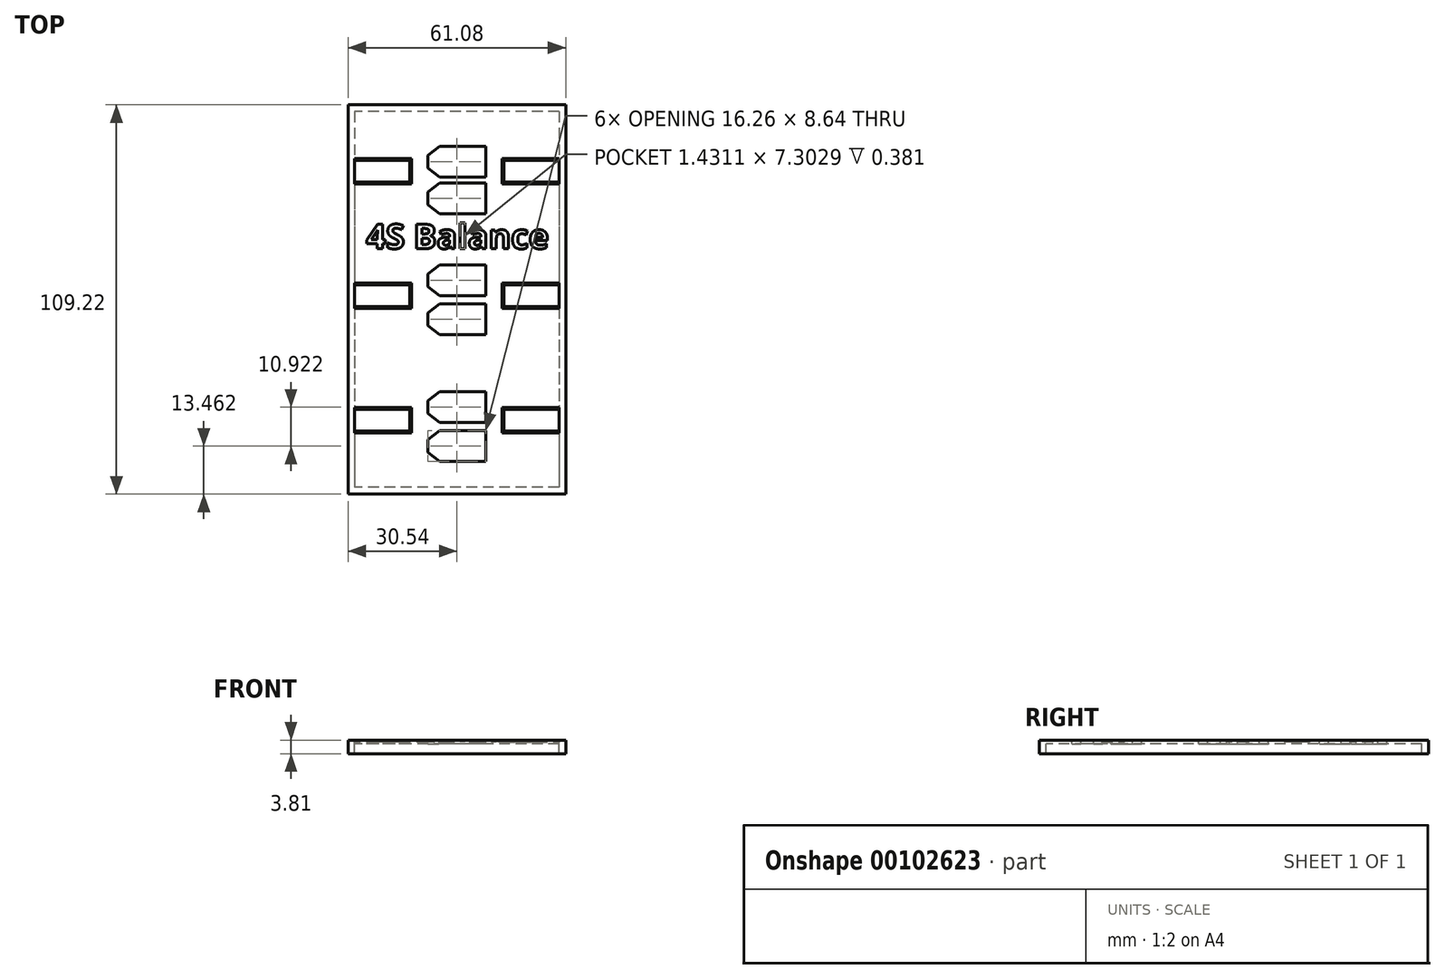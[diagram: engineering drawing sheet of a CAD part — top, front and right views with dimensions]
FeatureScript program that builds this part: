
annotation { "Feature Type Name" : "Feature", "Feature Type Description" : "" }
export const myFeature = defineFeature(function(context is Context, id is Id, definition is map)
    precondition{}
    {
        {
            var Q0;
            Q0=qCreatedBy(makeId("Top.planeOp"),FACE);
            var sketch = newSketch(context, id + "F0", { "sketchPlane" : qUnion([Q0])});
            skLineSegment(sketch, "E0.bottom", {"start": v(30.54, 54.61) * mm, "end": v(-30.54, 54.6) * mm});
            skLineSegment(sketch, "E0.top", {"start": v(30.54, -54.6) * mm, "end": v(-30.54, -54.61) * mm});
            skLineSegment(sketch, "E0.left", {"start": v(30.54, 54.61) * mm, "end": v(30.54, -54.6) * mm});
            skLineSegment(sketch, "E0.right", {"start": v(-30.54, 54.6) * mm, "end": v(-30.54, -54.61) * mm});
            skPoint(sketch, "E0.middle", {"position": v(0, 0) * mm});
            skLineSegment(sketch, "E1.bottom", {"start": v(28.7, 52.7) * mm, "end": v(-28.7, 52.7) * mm});
            skLineSegment(sketch, "E1.top", {"start": v(28.7, -52.7) * mm, "end": v(-28.7, -52.7) * mm});
            skLineSegment(sketch, "E1.left", {"start": v(28.7, 52.7) * mm, "end": v(28.7, -52.7) * mm});
            skLineSegment(sketch, "E1.right", {"start": v(-28.7, 52.7) * mm, "end": v(-28.7, -52.7) * mm});
            skLineSegment(sketch, "E2.bottom", {"start": v(8.13, -36.83) * mm, "end": v(-8.13, -36.83) * mm});
            skLineSegment(sketch, "E2.top", {"start": v(8.13, -45.47) * mm, "end": v(-8.13, -45.47) * mm});
            skLineSegment(sketch, "E2.left", {"start": v(8.13, -36.83) * mm, "end": v(8.13, -45.47) * mm});
            skLineSegment(sketch, "E2.right", {"start": v(-8.13, -36.83) * mm, "end": v(-8.13, -45.47) * mm});
            skPoint(sketch, "E2.middle", {"position": v(0, -41.15) * mm});
            skLineSegment(sketch, "E3.bottom", {"start": v(8.13, -34.54) * mm, "end": v(-8.13, -34.54) * mm});
            skLineSegment(sketch, "E3.top", {"start": v(8.13, -25.9) * mm, "end": v(-8.13, -25.9) * mm});
            skLineSegment(sketch, "E3.left", {"start": v(8.13, -34.54) * mm, "end": v(8.13, -25.9) * mm});
            skLineSegment(sketch, "E3.right", {"start": v(-8.13, -34.54) * mm, "end": v(-8.13, -25.9) * mm});
            skPoint(sketch, "E3.middle", {"position": v(0, -30.23) * mm});
            skLineSegment(sketch, "E4.bottom", {"start": v(8.13, -9.9) * mm, "end": v(-8.13, -9.9) * mm});
            skLineSegment(sketch, "E4.top", {"start": v(8.13, -1.27) * mm, "end": v(-8.13, -1.27) * mm});
            skLineSegment(sketch, "E4.left", {"start": v(8.13, -9.9) * mm, "end": v(8.13, -1.27) * mm});
            skLineSegment(sketch, "E4.right", {"start": v(-8.13, -9.9) * mm, "end": v(-8.13, -1.27) * mm});
            skPoint(sketch, "E4.middle", {"position": v(0, -5.59) * mm});
            skLineSegment(sketch, "E5.bottom", {"start": v(8.13, 1.02) * mm, "end": v(-8.13, 1.02) * mm});
            skLineSegment(sketch, "E5.top", {"start": v(8.13, 9.65) * mm, "end": v(-8.13, 9.65) * mm});
            skLineSegment(sketch, "E5.left", {"start": v(8.13, 1.02) * mm, "end": v(8.13, 9.65) * mm});
            skLineSegment(sketch, "E5.right", {"start": v(-8.13, 1.02) * mm, "end": v(-8.13, 9.65) * mm});
            skPoint(sketch, "E5.middle", {"position": v(0, 5.33) * mm});
            skLineSegment(sketch, "E6.bottom", {"start": v(8.13, 24) * mm, "end": v(-8.13, 24) * mm});
            skLineSegment(sketch, "E6.top", {"start": v(8.13, 32.64) * mm, "end": v(-8.13, 32.64) * mm});
            skLineSegment(sketch, "E6.left", {"start": v(8.13, 24) * mm, "end": v(8.13, 32.64) * mm});
            skLineSegment(sketch, "E6.right", {"start": v(-8.13, 24) * mm, "end": v(-8.13, 32.64) * mm});
            skPoint(sketch, "E6.middle", {"position": v(0, 28.32) * mm});
            skLineSegment(sketch, "E7.bottom", {"start": v(8.13, 34.29) * mm, "end": v(-8.13, 34.29) * mm});
            skLineSegment(sketch, "E7.top", {"start": v(8.13, 42.93) * mm, "end": v(-8.13, 42.93) * mm});
            skLineSegment(sketch, "E7.left", {"start": v(8.13, 34.3) * mm, "end": v(8.13, 42.93) * mm});
            skLineSegment(sketch, "E7.right", {"start": v(-8.13, 34.3) * mm, "end": v(-8.13, 42.93) * mm});
            skPoint(sketch, "E7.middle", {"position": v(0, 38.6) * mm});
            skLineSegment(sketch, "E8", {"start": v(-4.83, -45.47) * mm, "end": v(-8.13, -42.93) * mm});
            skLineSegment(sketch, "E9", {"start": v(-8.13, -39.37) * mm, "end": v(-4.83, -36.83) * mm});
            skLineSegment(sketch, "E10", {"start": v(-4.83, -34.54) * mm, "end": v(-8.13, -32) * mm});
            skLineSegment(sketch, "E11", {"start": v(-8.13, -28.45) * mm, "end": v(-4.83, -25.9) * mm});
            skLineSegment(sketch, "E12", {"start": v(-4.83, -9.9) * mm, "end": v(-8.13, -7.37) * mm});
            skLineSegment(sketch, "E13", {"start": v(-8.13, -3.81) * mm, "end": v(-4.83, -1.27) * mm});
            skLineSegment(sketch, "E14", {"start": v(-4.83, 1.02) * mm, "end": v(-8.13, 3.56) * mm});
            skLineSegment(sketch, "E15", {"start": v(-8.13, 7.11) * mm, "end": v(-4.83, 9.65) * mm});
            skLineSegment(sketch, "E16", {"start": v(-4.83, 24) * mm, "end": v(-8.13, 26.54) * mm});
            skLineSegment(sketch, "E17", {"start": v(-8.13, 30.1) * mm, "end": v(-4.83, 32.64) * mm});
            skLineSegment(sketch, "E18", {"start": v(-4.83, 34.3) * mm, "end": v(-8.13, 36.83) * mm});
            skLineSegment(sketch, "E19", {"start": v(-8.13, 40.39) * mm, "end": v(-4.83, 42.93) * mm});
            skLineSegment(sketch, "E20.bottom", {"start": v(28.7, -2.03) * mm, "end": v(13.2, -2.03) * mm});
            skLineSegment(sketch, "E20.top", {"start": v(28.7, 4.06) * mm, "end": v(13.2, 4.06) * mm});
            skLineSegment(sketch, "E20.left", {"start": v(28.7, -2.03) * mm, "end": v(28.7, 4.06) * mm});
            skLineSegment(sketch, "E20.right", {"start": v(13.2, -2.03) * mm, "end": v(13.2, 4.06) * mm});
            skPoint(sketch, "E20.middle", {"position": v(20.96, 1.02) * mm});
            skLineSegment(sketch, "E21.bottom", {"start": v(28.7, 32.9) * mm, "end": v(13.2, 32.9) * mm});
            skLineSegment(sketch, "E21.top", {"start": v(28.7, 38.99) * mm, "end": v(13.2, 38.99) * mm});
            skLineSegment(sketch, "E21.left", {"start": v(28.7, 32.9) * mm, "end": v(28.7, 38.99) * mm});
            skLineSegment(sketch, "E21.right", {"start": v(13.2, 32.9) * mm, "end": v(13.2, 38.99) * mm});
            skPoint(sketch, "E21.middle", {"position": v(20.95, 35.94) * mm});
            skLineSegment(sketch, "E22.bottom", {"start": v(28.7, -30.86) * mm, "end": v(13.2, -30.86) * mm});
            skLineSegment(sketch, "E22.top", {"start": v(28.7, -36.96) * mm, "end": v(13.2, -36.96) * mm});
            skLineSegment(sketch, "E22.left", {"start": v(28.7, -30.86) * mm, "end": v(28.7, -36.96) * mm});
            skLineSegment(sketch, "E22.right", {"start": v(13.2, -30.86) * mm, "end": v(13.2, -36.96) * mm});
            skPoint(sketch, "E22.middle", {"position": v(20.96, -33.9) * mm});
            skLineSegment(sketch, "E23.bottom", {"start": v(-13.2, -30.86) * mm, "end": v(-28.7, -30.86) * mm});
            skLineSegment(sketch, "E23.top", {"start": v(-13.2, -36.96) * mm, "end": v(-28.7, -36.96) * mm});
            skLineSegment(sketch, "E23.left", {"start": v(-13.2, -30.86) * mm, "end": v(-13.2, -36.96) * mm});
            skLineSegment(sketch, "E23.right", {"start": v(-28.7, -30.86) * mm, "end": v(-28.7, -36.96) * mm});
            skPoint(sketch, "E23.middle", {"position": v(-20.96, -33.9) * mm});
            skLineSegment(sketch, "E24.bottom", {"start": v(-13.2, 4.06) * mm, "end": v(-28.7, 4.06) * mm});
            skLineSegment(sketch, "E24.top", {"start": v(-13.2, -2.03) * mm, "end": v(-28.7, -2.03) * mm});
            skLineSegment(sketch, "E24.left", {"start": v(-13.2, 4.06) * mm, "end": v(-13.2, -2.03) * mm});
            skLineSegment(sketch, "E24.right", {"start": v(-28.7, 4.06) * mm, "end": v(-28.7, -2.03) * mm});
            skPoint(sketch, "E24.middle", {"position": v(-20.95, 1.02) * mm});
            skLineSegment(sketch, "E25.bottom", {"start": v(-13.2, 38.99) * mm, "end": v(-28.7, 38.99) * mm});
            skLineSegment(sketch, "E25.top", {"start": v(-13.2, 32.9) * mm, "end": v(-28.7, 32.9) * mm});
            skLineSegment(sketch, "E25.left", {"start": v(-13.2, 38.99) * mm, "end": v(-13.2, 32.9) * mm});
            skLineSegment(sketch, "E25.right", {"start": v(-28.7, 38.99) * mm, "end": v(-28.7, 32.9) * mm});
            skPoint(sketch, "E25.middle", {"position": v(-20.95, 35.94) * mm});
            skSolve(sketch);
        }
        {
            var Q0;
            Q0=makeQuery(id+"F0.imprint","IMPRINT",FACE,{"disambiguationData":[TD([[makeQuery(id+"F0.imprint","IMPRINT",EDGE,{"derivedFrom":sQuery(id+"F0.wireOp",EDGE,"E1.bottom")}),1.0]])]});
            var Q1;
            {var subQ3=sQuery(id+"F0.wireOp",EDGE,"E8");Q1=makeQuery(id+"F0.imprint","IMPRINT",FACE,{"disambiguationData":[TD([[makeQuery(id+"F0.imprint","IMPRINT",EDGE,{"derivedFrom":subQ3}),1.0]])]});}
            var Q2;
            {var subQ3=sQuery(id+"F0.wireOp",EDGE,"E9");Q2=makeQuery(id+"F0.imprint","IMPRINT",FACE,{"disambiguationData":[TD([[makeQuery(id+"F0.imprint","IMPRINT",EDGE,{"derivedFrom":subQ3}),1.0]])]});}
            var Q3;
            {var subQ3=sQuery(id+"F0.wireOp",EDGE,"E10");Q3=makeQuery(id+"F0.imprint","IMPRINT",FACE,{"disambiguationData":[TD([[makeQuery(id+"F0.imprint","IMPRINT",EDGE,{"derivedFrom":subQ3}),1.0]])]});}
            var Q4;
            {var subQ3=sQuery(id+"F0.wireOp",EDGE,"E11");Q4=makeQuery(id+"F0.imprint","IMPRINT",FACE,{"disambiguationData":[TD([[makeQuery(id+"F0.imprint","IMPRINT",EDGE,{"derivedFrom":subQ3}),1.0]])]});}
            var Q5;
            {var subQ3=sQuery(id+"F0.wireOp",EDGE,"E12");Q5=makeQuery(id+"F0.imprint","IMPRINT",FACE,{"disambiguationData":[TD([[makeQuery(id+"F0.imprint","IMPRINT",EDGE,{"derivedFrom":subQ3}),1.0]])]});}
            var Q6;
            {var subQ3=sQuery(id+"F0.wireOp",EDGE,"E13");Q6=makeQuery(id+"F0.imprint","IMPRINT",FACE,{"disambiguationData":[TD([[makeQuery(id+"F0.imprint","IMPRINT",EDGE,{"derivedFrom":subQ3}),1.0]])]});}
            var Q7;
            {var subQ3=sQuery(id+"F0.wireOp",EDGE,"E14");Q7=makeQuery(id+"F0.imprint","IMPRINT",FACE,{"disambiguationData":[TD([[makeQuery(id+"F0.imprint","IMPRINT",EDGE,{"derivedFrom":subQ3}),1.0]])]});}
            var Q8;
            {var subQ3=sQuery(id+"F0.wireOp",EDGE,"E15");Q8=makeQuery(id+"F0.imprint","IMPRINT",FACE,{"disambiguationData":[TD([[makeQuery(id+"F0.imprint","IMPRINT",EDGE,{"derivedFrom":subQ3}),1.0]])]});}
            var Q9;
            {var subQ3=sQuery(id+"F0.wireOp",EDGE,"E16");Q9=makeQuery(id+"F0.imprint","IMPRINT",FACE,{"disambiguationData":[TD([[makeQuery(id+"F0.imprint","IMPRINT",EDGE,{"derivedFrom":subQ3}),1.0]])]});}
            var Q10;
            {var subQ3=sQuery(id+"F0.wireOp",EDGE,"E17");Q10=makeQuery(id+"F0.imprint","IMPRINT",FACE,{"disambiguationData":[TD([[makeQuery(id+"F0.imprint","IMPRINT",EDGE,{"derivedFrom":subQ3}),1.0]])]});}
            var Q11;
            {var subQ3=sQuery(id+"F0.wireOp",EDGE,"E18");Q11=makeQuery(id+"F0.imprint","IMPRINT",FACE,{"disambiguationData":[TD([[makeQuery(id+"F0.imprint","IMPRINT",EDGE,{"derivedFrom":subQ3}),1.0]])]});}
            var Q12;
            {var subQ3=sQuery(id+"F0.wireOp",EDGE,"E19");Q12=makeQuery(id+"F0.imprint","IMPRINT",FACE,{"disambiguationData":[TD([[makeQuery(id+"F0.imprint","IMPRINT",EDGE,{"derivedFrom":subQ3}),1.0]])]});}
            extrude(context, id + "F1", {"entities" : qUnion([Q0, Q1, Q2, Q3, Q4, Q5, Q6, Q7, Q8, Q9, Q10, Q11, Q12]), "oppositeDirection" : true, "depth" : 1.02 * mm});
        }
        {
            var Q0;
            Q0=makeQuery(id+"F0.imprint","IMPRINT",FACE,{"disambiguationData":[TD([[makeQuery(id+"F0.imprint","IMPRINT",EDGE,{"derivedFrom":sQuery(id+"F0.wireOp",EDGE,"E0.bottom")}),1.0]])]});
            extrude(context, id + "F2", {"entities" : qUnion([Q0]), "operationType" : NewBodyOperationType.ADD, "oppositeDirection" : true, "depth" : 3.8 * mm});
        }
        {
            var Q0;
            {var subQ0=sQuery(id+"F0.wireOp",EDGE,"E25.top");var subQ1=sQuery(id+"F0.wireOp",EDGE,"E25.bottom");var subQ2=sQuery(id+"F0.wireOp",EDGE,"E24.top");var subQ3=sQuery(id+"F0.wireOp",EDGE,"E24.bottom");var subQ4=sQuery(id+"F0.wireOp",EDGE,"E23.top");var subQ5=sQuery(id+"F0.wireOp",EDGE,"E23.bottom");var subQ6=sQuery(id+"F0.wireOp",EDGE,"E22.top");var subQ7=sQuery(id+"F0.wireOp",EDGE,"E22.bottom");var subQ8=sQuery(id+"F0.wireOp",EDGE,"E21.top");var subQ9=sQuery(id+"F0.wireOp",EDGE,"E21.bottom");var subQ10=sQuery(id+"F0.wireOp",EDGE,"E20.top");var subQ11=sQuery(id+"F0.wireOp",EDGE,"E20.bottom");var subQ12=sQuery(id+"F0.wireOp",EDGE,"E1.right");var subQ13=sQuery(id+"F0.wireOp",EDGE,"E1.left");var subQ14=sQuery(id+"F0.wireOp",EDGE,"E1.top");var subQ15=sQuery(id+"F0.wireOp",EDGE,"E1.bottom");Q0=makeQuery(id+"F2.boolean.opBoolean","MERGE",FACE,{"derivedFrom":[makeQuery(id+"F1.opExtrude","CAP_FACE",FACE,{"disambiguationData":[OSD([subQ15,subQ14,subQ13,subQ12,sQuery(id+"F0.wireOp",EDGE,"E2.bottom"),sQuery(id+"F0.wireOp",EDGE,"E2.top"),sQuery(id+"F0.wireOp",EDGE,"E2.left"),sQuery(id+"F0.wireOp",EDGE,"E2.right"),sQuery(id+"F0.wireOp",EDGE,"E3.bottom"),sQuery(id+"F0.wireOp",EDGE,"E3.top"),sQuery(id+"F0.wireOp",EDGE,"E3.left"),sQuery(id+"F0.wireOp",EDGE,"E3.right"),sQuery(id+"F0.wireOp",EDGE,"E4.bottom"),sQuery(id+"F0.wireOp",EDGE,"E4.top"),sQuery(id+"F0.wireOp",EDGE,"E4.left"),sQuery(id+"F0.wireOp",EDGE,"E4.right"),sQuery(id+"F0.wireOp",EDGE,"E5.bottom"),sQuery(id+"F0.wireOp",EDGE,"E5.top"),sQuery(id+"F0.wireOp",EDGE,"E5.left"),sQuery(id+"F0.wireOp",EDGE,"E5.right"),sQuery(id+"F0.wireOp",EDGE,"E6.bottom"),sQuery(id+"F0.wireOp",EDGE,"E6.top"),sQuery(id+"F0.wireOp",EDGE,"E6.left"),sQuery(id+"F0.wireOp",EDGE,"E6.right"),sQuery(id+"F0.wireOp",EDGE,"E7.bottom"),sQuery(id+"F0.wireOp",EDGE,"E7.top"),sQuery(id+"F0.wireOp",EDGE,"E7.left"),sQuery(id+"F0.wireOp",EDGE,"E7.right"),sQuery(id+"F0.wireOp",EDGE,"E8"),sQuery(id+"F0.wireOp",EDGE,"E9"),sQuery(id+"F0.wireOp",EDGE,"E10"),sQuery(id+"F0.wireOp",EDGE,"E11"),sQuery(id+"F0.wireOp",EDGE,"E12"),sQuery(id+"F0.wireOp",EDGE,"E13"),sQuery(id+"F0.wireOp",EDGE,"E14"),sQuery(id+"F0.wireOp",EDGE,"E15"),sQuery(id+"F0.wireOp",EDGE,"E16"),sQuery(id+"F0.wireOp",EDGE,"E17"),sQuery(id+"F0.wireOp",EDGE,"E18"),sQuery(id+"F0.wireOp",EDGE,"E19"),subQ11,subQ10,sQuery(id+"F0.wireOp",EDGE,"E20.right"),subQ9,subQ8,sQuery(id+"F0.wireOp",EDGE,"E21.right"),subQ7,subQ6,sQuery(id+"F0.wireOp",EDGE,"E22.right"),subQ5,subQ4,sQuery(id+"F0.wireOp",EDGE,"E23.left"),subQ3,subQ2,sQuery(id+"F0.wireOp",EDGE,"E24.left"),subQ1,subQ0,sQuery(id+"F0.wireOp",EDGE,"E25.left")])],"isStart":true}),makeQuery(id+"F2.opExtrude","CAP_FACE",FACE,{"disambiguationData":[OSD([sQuery(id+"F0.wireOp",EDGE,"E0.bottom"),sQuery(id+"F0.wireOp",EDGE,"E0.top"),sQuery(id+"F0.wireOp",EDGE,"E0.left"),sQuery(id+"F0.wireOp",EDGE,"E0.right"),subQ15,subQ14,subQ13,subQ12,subQ11,subQ10,sQuery(id+"F0.wireOp",EDGE,"E20.left"),subQ9,subQ8,sQuery(id+"F0.wireOp",EDGE,"E21.left"),subQ7,subQ6,sQuery(id+"F0.wireOp",EDGE,"E22.left"),subQ5,subQ4,sQuery(id+"F0.wireOp",EDGE,"E23.right"),subQ3,subQ2,sQuery(id+"F0.wireOp",EDGE,"E24.right"),subQ1,subQ0,sQuery(id+"F0.wireOp",EDGE,"E25.right")])],"isStart":true})]});}
            var sketch = newSketch(context, id + "F3", { "sketchPlane" : qUnion([Q0])});
            skText(sketch, "E26", { "text": "4S Balance", "fontName": "OpenSans-Bold.ttf"});
            const initialGuessF3  = {"E26": [-0.0254, 0.01424, 1, 0, 0.00692]};
            skSetInitialGuess(sketch, initialGuessF3);
            skSolve(sketch);
        }
        {
            var Q0;
            Q0 = qSketchRegion(id + "F3", true);
            extrude(context, id + "F4", {"entities" : qUnion([Q0]), "operationType" : NewBodyOperationType.REMOVE, "oppositeDirection" : true, "depth" : 0.38 * mm});
        }
        {
            var Q0;
            {var subQ0=sQuery(id+"F0.wireOp",EDGE,"E20.top");Q0=makeQuery(id+"F2.boolean.opBoolean","MERGE",EDGE,{"derivedFrom":[makeQuery(id+"F1.opExtrude","CAP_EDGE",EDGE,{"disambiguationData":[OSD([subQ0])],"isStart":true}),makeQuery(id+"F2.opExtrude","CAP_EDGE",EDGE,{"disambiguationData":[OSD([subQ0])],"isStart":true})]});}
            var Q1;
            Q1=makeQuery(id+"F1.opExtrude","CAP_EDGE",EDGE,{"disambiguationData":[OSD([sQuery(id+"F0.wireOp",EDGE,"E20.right")])],"isStart":true});
            var Q2;
            {var subQ0=sQuery(id+"F0.wireOp",EDGE,"E20.bottom");Q2=makeQuery(id+"F2.boolean.opBoolean","MERGE",EDGE,{"derivedFrom":[makeQuery(id+"F1.opExtrude","CAP_EDGE",EDGE,{"disambiguationData":[OSD([subQ0])],"isStart":true}),makeQuery(id+"F2.opExtrude","CAP_EDGE",EDGE,{"disambiguationData":[OSD([subQ0])],"isStart":true})]});}
            var Q3;
            Q3=makeQuery(id+"F2.opExtrude","CAP_EDGE",EDGE,{"disambiguationData":[OSD([sQuery(id+"F0.wireOp",EDGE,"E20.left")])],"isStart":true});
            var Q4;
            {var subQ0=sQuery(id+"F0.wireOp",EDGE,"E21.bottom");Q4=makeQuery(id+"F2.boolean.opBoolean","MERGE",EDGE,{"derivedFrom":[makeQuery(id+"F1.opExtrude","CAP_EDGE",EDGE,{"disambiguationData":[OSD([subQ0])],"isStart":true}),makeQuery(id+"F2.opExtrude","CAP_EDGE",EDGE,{"disambiguationData":[OSD([subQ0])],"isStart":true})]});}
            var Q5;
            {var subQ0=sQuery(id+"F0.wireOp",EDGE,"E21.top");Q5=makeQuery(id+"F2.boolean.opBoolean","MERGE",EDGE,{"derivedFrom":[makeQuery(id+"F1.opExtrude","CAP_EDGE",EDGE,{"disambiguationData":[OSD([subQ0])],"isStart":true}),makeQuery(id+"F2.opExtrude","CAP_EDGE",EDGE,{"disambiguationData":[OSD([subQ0])],"isStart":true})]});}
            var Q6;
            Q6=makeQuery(id+"F1.opExtrude","CAP_EDGE",EDGE,{"disambiguationData":[OSD([sQuery(id+"F0.wireOp",EDGE,"E21.right")])],"isStart":true});
            var Q7;
            Q7=makeQuery(id+"F2.opExtrude","CAP_EDGE",EDGE,{"disambiguationData":[OSD([sQuery(id+"F0.wireOp",EDGE,"E21.left")])],"isStart":true});
            var Q8;
            {var subQ0=sQuery(id+"F0.wireOp",EDGE,"E22.bottom");Q8=makeQuery(id+"F2.boolean.opBoolean","MERGE",EDGE,{"derivedFrom":[makeQuery(id+"F1.opExtrude","CAP_EDGE",EDGE,{"disambiguationData":[OSD([subQ0])],"isStart":true}),makeQuery(id+"F2.opExtrude","CAP_EDGE",EDGE,{"disambiguationData":[OSD([subQ0])],"isStart":true})]});}
            var Q9;
            {var subQ0=sQuery(id+"F0.wireOp",EDGE,"E22.top");Q9=makeQuery(id+"F2.boolean.opBoolean","MERGE",EDGE,{"derivedFrom":[makeQuery(id+"F1.opExtrude","CAP_EDGE",EDGE,{"disambiguationData":[OSD([subQ0])],"isStart":true}),makeQuery(id+"F2.opExtrude","CAP_EDGE",EDGE,{"disambiguationData":[OSD([subQ0])],"isStart":true})]});}
            var Q10;
            Q10=makeQuery(id+"F1.opExtrude","CAP_EDGE",EDGE,{"disambiguationData":[OSD([sQuery(id+"F0.wireOp",EDGE,"E22.right")])],"isStart":true});
            var Q11;
            Q11=makeQuery(id+"F2.opExtrude","CAP_EDGE",EDGE,{"disambiguationData":[OSD([sQuery(id+"F0.wireOp",EDGE,"E22.left")])],"isStart":true});
            var Q12;
            {var subQ0=sQuery(id+"F0.wireOp",EDGE,"E23.top");Q12=makeQuery(id+"F2.boolean.opBoolean","MERGE",EDGE,{"derivedFrom":[makeQuery(id+"F1.opExtrude","CAP_EDGE",EDGE,{"disambiguationData":[OSD([subQ0])],"isStart":true}),makeQuery(id+"F2.opExtrude","CAP_EDGE",EDGE,{"disambiguationData":[OSD([subQ0])],"isStart":true})]});}
            var Q13;
            {var subQ0=sQuery(id+"F0.wireOp",EDGE,"E23.bottom");Q13=makeQuery(id+"F2.boolean.opBoolean","MERGE",EDGE,{"derivedFrom":[makeQuery(id+"F1.opExtrude","CAP_EDGE",EDGE,{"disambiguationData":[OSD([subQ0])],"isStart":true}),makeQuery(id+"F2.opExtrude","CAP_EDGE",EDGE,{"disambiguationData":[OSD([subQ0])],"isStart":true})]});}
            var Q14;
            Q14=makeQuery(id+"F1.opExtrude","CAP_EDGE",EDGE,{"disambiguationData":[OSD([sQuery(id+"F0.wireOp",EDGE,"E23.left")])],"isStart":true});
            var Q15;
            Q15=makeQuery(id+"F2.opExtrude","CAP_EDGE",EDGE,{"disambiguationData":[OSD([sQuery(id+"F0.wireOp",EDGE,"E23.right")])],"isStart":true});
            var Q16;
            {var subQ0=sQuery(id+"F0.wireOp",EDGE,"E24.top");Q16=makeQuery(id+"F2.boolean.opBoolean","MERGE",EDGE,{"derivedFrom":[makeQuery(id+"F1.opExtrude","CAP_EDGE",EDGE,{"disambiguationData":[OSD([subQ0])],"isStart":true}),makeQuery(id+"F2.opExtrude","CAP_EDGE",EDGE,{"disambiguationData":[OSD([subQ0])],"isStart":true})]});}
            var Q17;
            {var subQ0=sQuery(id+"F0.wireOp",EDGE,"E24.bottom");Q17=makeQuery(id+"F2.boolean.opBoolean","MERGE",EDGE,{"derivedFrom":[makeQuery(id+"F1.opExtrude","CAP_EDGE",EDGE,{"disambiguationData":[OSD([subQ0])],"isStart":true}),makeQuery(id+"F2.opExtrude","CAP_EDGE",EDGE,{"disambiguationData":[OSD([subQ0])],"isStart":true})]});}
            var Q18;
            Q18=makeQuery(id+"F1.opExtrude","CAP_EDGE",EDGE,{"disambiguationData":[OSD([sQuery(id+"F0.wireOp",EDGE,"E24.left")])],"isStart":true});
            var Q19;
            Q19=makeQuery(id+"F2.opExtrude","CAP_EDGE",EDGE,{"disambiguationData":[OSD([sQuery(id+"F0.wireOp",EDGE,"E24.right")])],"isStart":true});
            var Q20;
            {var subQ0=sQuery(id+"F0.wireOp",EDGE,"E25.top");Q20=makeQuery(id+"F2.boolean.opBoolean","MERGE",EDGE,{"derivedFrom":[makeQuery(id+"F1.opExtrude","CAP_EDGE",EDGE,{"disambiguationData":[OSD([subQ0])],"isStart":true}),makeQuery(id+"F2.opExtrude","CAP_EDGE",EDGE,{"disambiguationData":[OSD([subQ0])],"isStart":true})]});}
            var Q21;
            {var subQ0=sQuery(id+"F0.wireOp",EDGE,"E25.bottom");Q21=makeQuery(id+"F2.boolean.opBoolean","MERGE",EDGE,{"derivedFrom":[makeQuery(id+"F1.opExtrude","CAP_EDGE",EDGE,{"disambiguationData":[OSD([subQ0])],"isStart":true}),makeQuery(id+"F2.opExtrude","CAP_EDGE",EDGE,{"disambiguationData":[OSD([subQ0])],"isStart":true})]});}
            var Q22;
            Q22=makeQuery(id+"F1.opExtrude","CAP_EDGE",EDGE,{"disambiguationData":[OSD([sQuery(id+"F0.wireOp",EDGE,"E25.left")])],"isStart":true});
            var Q23;
            Q23=makeQuery(id+"F2.opExtrude","CAP_EDGE",EDGE,{"disambiguationData":[OSD([sQuery(id+"F0.wireOp",EDGE,"E25.right")])],"isStart":true});
            chamfer(context, id + "F5", {"entities" : qUnion([Q0, Q1, Q2, Q3, Q4, Q5, Q6, Q7, Q8, Q9, Q10, Q11, Q12, Q13, Q14, Q15, Q16, Q17, Q18, Q19, Q20, Q21, Q22, Q23]), "width" : 0.5 * mm, "tangentPropagation" : true});
        }
    });
